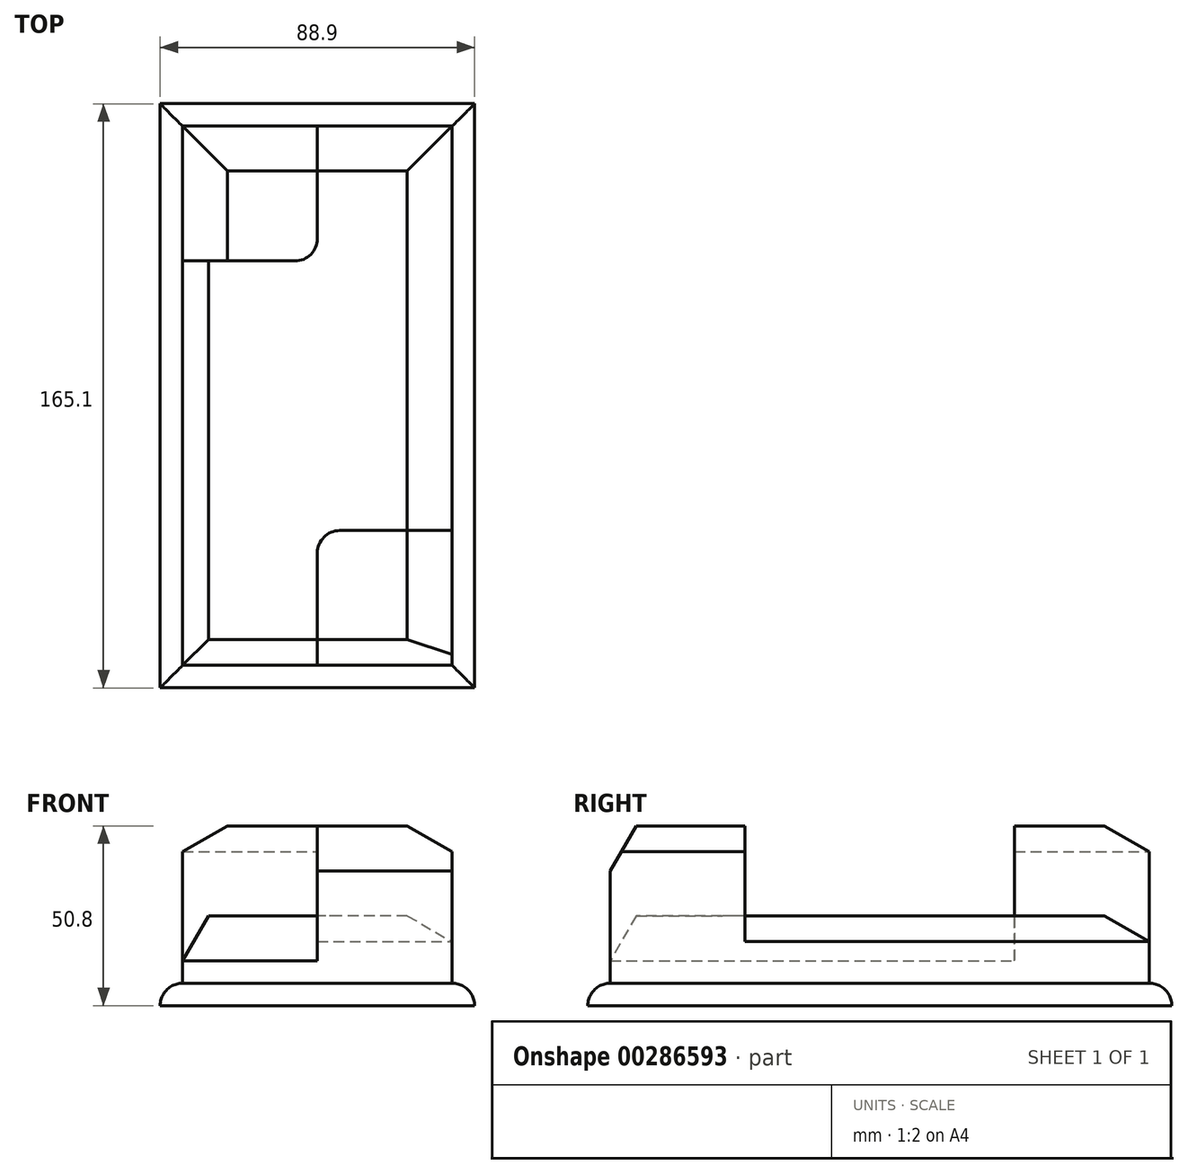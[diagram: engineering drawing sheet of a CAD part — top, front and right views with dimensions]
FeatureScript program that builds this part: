
annotation { "Feature Type Name" : "Feature", "Feature Type Description" : "" }
export const myFeature = defineFeature(function(context is Context, id is Id, definition is map)
    precondition{}
    {
        {
            var Q0;
            Q0=qCreatedBy(makeId("Top.planeOp"),FACE);
            var sketch = newSketch(context, id + "F0", { "sketchPlane" : qUnion([Q0])});
            skLineSegment(sketch, "E0.bottom", {"start": v(-44.45, 77.72) * mm, "end": v(31.75, 77.72) * mm});
            skLineSegment(sketch, "E0.top", {"start": v(-44.45, -74.68) * mm, "end": v(31.75, -74.68) * mm});
            skLineSegment(sketch, "E0.left", {"start": v(-44.45, 77.72) * mm, "end": v(-44.45, -74.68) * mm});
            skLineSegment(sketch, "E0.right", {"start": v(31.75, 77.72) * mm, "end": v(31.75, -74.68) * mm});
            skArc(sketch, "E1", {"start": v(-12.7, 39.62) * mm, "mid": v(-8.2, 41.48) * mm, "end": v(-6.35, 45.97) * mm});
            skArc(sketch, "E2", {"start": v(0, -36.58) * mm, "mid": v(-4.5, -38.44) * mm, "end": v(-6.35, -42.93) * mm});
            skLineSegment(sketch, "E3", {"start": v(-6.35, 45.97) * mm, "end": v(-6.35, 77.72) * mm});
            skLineSegment(sketch, "E4", {"start": v(-44.45, 39.62) * mm, "end": v(-12.7, 39.62) * mm});
            skLineSegment(sketch, "E5", {"start": v(-6.35, -74.68) * mm, "end": v(-6.35, -42.93) * mm});
            skLineSegment(sketch, "E6", {"start": v(31.75, -36.58) * mm, "end": v(0, -36.58) * mm});
            skLineSegment(sketch, "E7.0", {"start": v(-50.8, 84.07) * mm, "end": v(38.1, 84.07) * mm});
            skLineSegment(sketch, "E7.1", {"start": v(-50.8, 84.07) * mm, "end": v(-50.8, -81.03) * mm});
            skLineSegment(sketch, "E7.2", {"start": v(-50.8, -81.03) * mm, "end": v(38.1, -81.03) * mm});
            skLineSegment(sketch, "E7.3", {"start": v(38.1, 84.07) * mm, "end": v(38.1, -81.03) * mm});
            skLineSegment(sketch, "E8", {"start": v(-44.45, 58.7) * mm, "end": v(-6.35, 58.7) * mm, "construction": true});
            skLineSegment(sketch, "E9", {"start": v(-24.28, 77.72) * mm, "end": v(-24.28, 39.62) * mm, "construction": true});
            skLineSegment(sketch, "E10", {"start": v(26.92, -36.58) * mm, "end": v(26.92, -74.68) * mm, "construction": true});
            skLineSegment(sketch, "E11", {"start": v(-6.35, -58.8) * mm, "end": v(31.75, -58.8) * mm, "construction": true});
            skSolve(sketch);
        }
        {
            var Q0;
            Q0=makeQuery(id+"F0.imprint","IMPRINT",FACE,{"disambiguationData":[TD([[makeQuery(id+"F0.imprint","IMPRINT",EDGE,{"derivedFrom":sQuery(id+"F0.wireOp",EDGE,"E7.0")}),-1.0]])]});
            var Q1;
            Q1=makeQuery(id+"F0.imprint","IMPRINT",FACE,{"disambiguationData":[TD([[makeQuery(id+"F0.imprint","IMPRINT",EDGE,{"derivedFrom":sQuery(id+"F0.wireOp",EDGE,"E1")}),-1.0]])]});
            var Q2;
            Q2=makeQuery(id+"F0.imprint","IMPRINT",FACE,{"disambiguationData":[TD([[makeQuery(id+"F0.imprint","IMPRINT",EDGE,{"derivedFrom":sQuery(id+"F0.wireOp",EDGE,"E1")}),1.0]])]});
            var Q3;
            Q3=makeQuery(id+"F0.imprint","IMPRINT",FACE,{"disambiguationData":[TD([[makeQuery(id+"F0.imprint","IMPRINT",EDGE,{"derivedFrom":sQuery(id+"F0.wireOp",EDGE,"E2")}),1.0]])]});
            extrude(context, id + "F1", {"entities" : qUnion([Q0, Q1, Q2, Q3]), "depth" : 6.35 * mm});
        }
        {
            var Q0;
            Q0=makeQuery(id+"F0.imprint","IMPRINT",FACE,{"disambiguationData":[TD([[makeQuery(id+"F0.imprint","IMPRINT",EDGE,{"derivedFrom":sQuery(id+"F0.wireOp",EDGE,"E1")}),-1.0]])]});
            extrude(context, id + "F2", {"entities" : qUnion([Q0]), "operationType" : NewBodyOperationType.ADD, "depth" : 25.4 * mm});
        }
        {
            var Q0;
            Q0=makeQuery(id+"F0.imprint","IMPRINT",FACE,{"disambiguationData":[TD([[makeQuery(id+"F0.imprint","IMPRINT",EDGE,{"derivedFrom":sQuery(id+"F0.wireOp",EDGE,"E1")}),1.0]])]});
            var Q1;
            Q1=makeQuery(id+"F0.imprint","IMPRINT",FACE,{"disambiguationData":[TD([[makeQuery(id+"F0.imprint","IMPRINT",EDGE,{"derivedFrom":sQuery(id+"F0.wireOp",EDGE,"E2")}),1.0]])]});
            extrude(context, id + "F3", {"entities" : qUnion([Q0, Q1]), "operationType" : NewBodyOperationType.ADD, "depth" : 50.8 * mm});
        }
        {
            var Q0;
            Q0=makeQuery(id+"F1.opExtrude","CAP_EDGE",EDGE,{"disambiguationData":[OSD([sQuery(id+"F0.wireOp",EDGE,"E7.3")])],"isStart":false});
            var Q1;
            Q1=makeQuery(id+"F1.opExtrude","CAP_EDGE",EDGE,{"disambiguationData":[OSD([sQuery(id+"F0.wireOp",EDGE,"E7.2")])],"isStart":false});
            var Q2;
            Q2=makeQuery(id+"F1.opExtrude","CAP_EDGE",EDGE,{"disambiguationData":[OSD([sQuery(id+"F0.wireOp",EDGE,"E7.0")])],"isStart":false});
            var Q3;
            Q3=makeQuery(id+"F1.opExtrude","CAP_EDGE",EDGE,{"disambiguationData":[OSD([sQuery(id+"F0.wireOp",EDGE,"E7.1")])],"isStart":false});
            fillet(context, id + "F4", {"entities" : qUnion([Q0, Q1, Q2, Q3]), "radius" : 6.35 * mm, "tangentPropagation" : true, "allowEdgeOverflow" : false});
        }
        {
            var Q0;
            Q0=makeQuery(id+"F3.opExtrude","CAP_EDGE",EDGE,{"disambiguationData":[OSD([sQuery(id+"F0.wireOp",EDGE,"E0.bottom")])],"isStart":false});
            var Q1;
            Q1=makeQuery(id+"F3.opExtrude","CAP_EDGE",EDGE,{"disambiguationData":[OSD([sQuery(id+"F0.wireOp",EDGE,"E0.right")])],"isStart":false});
            var Q2;
            Q2=makeQuery(id+"F3.opExtrude","CAP_EDGE",EDGE,{"disambiguationData":[OSD([sQuery(id+"F0.wireOp",EDGE,"E0.top")])],"isStart":false});
            var Q3;
            Q3=makeQuery(id+"F3.opExtrude","CAP_EDGE",EDGE,{"disambiguationData":[OSD([sQuery(id+"F0.wireOp",EDGE,"E0.left")])],"isStart":false});
            var Q4;
            Q4=makeQuery(id+"F2.opExtrude","CAP_EDGE",EDGE,{"disambiguationData":[OSD([sQuery(id+"F0.wireOp",EDGE,"E0.right")])],"isStart":false});
            var Q5;
            Q5=makeQuery(id+"F2.opExtrude","CAP_EDGE",EDGE,{"disambiguationData":[OSD([sQuery(id+"F0.wireOp",EDGE,"E0.bottom")])],"isStart":false});
            var Q6;
            Q6=makeQuery(id+"F2.opExtrude","CAP_EDGE",EDGE,{"disambiguationData":[OSD([sQuery(id+"F0.wireOp",EDGE,"E0.left")])],"isStart":false});
            var Q7;
            Q7=makeQuery(id+"F2.opExtrude","CAP_EDGE",EDGE,{"disambiguationData":[OSD([sQuery(id+"F0.wireOp",EDGE,"E0.top")])],"isStart":false});
            chamfer(context, id + "F5", {"entities" : qUnion([Q0, Q1, Q2, Q3, Q4, Q5, Q6, Q7]), "chamferType" : ChamferType.OFFSET_ANGLE, "width" : 12.7 * mm, "oppositeDirection" : true, "angle" : 30 * degree, "tangentPropagation" : true});
        }
    });
